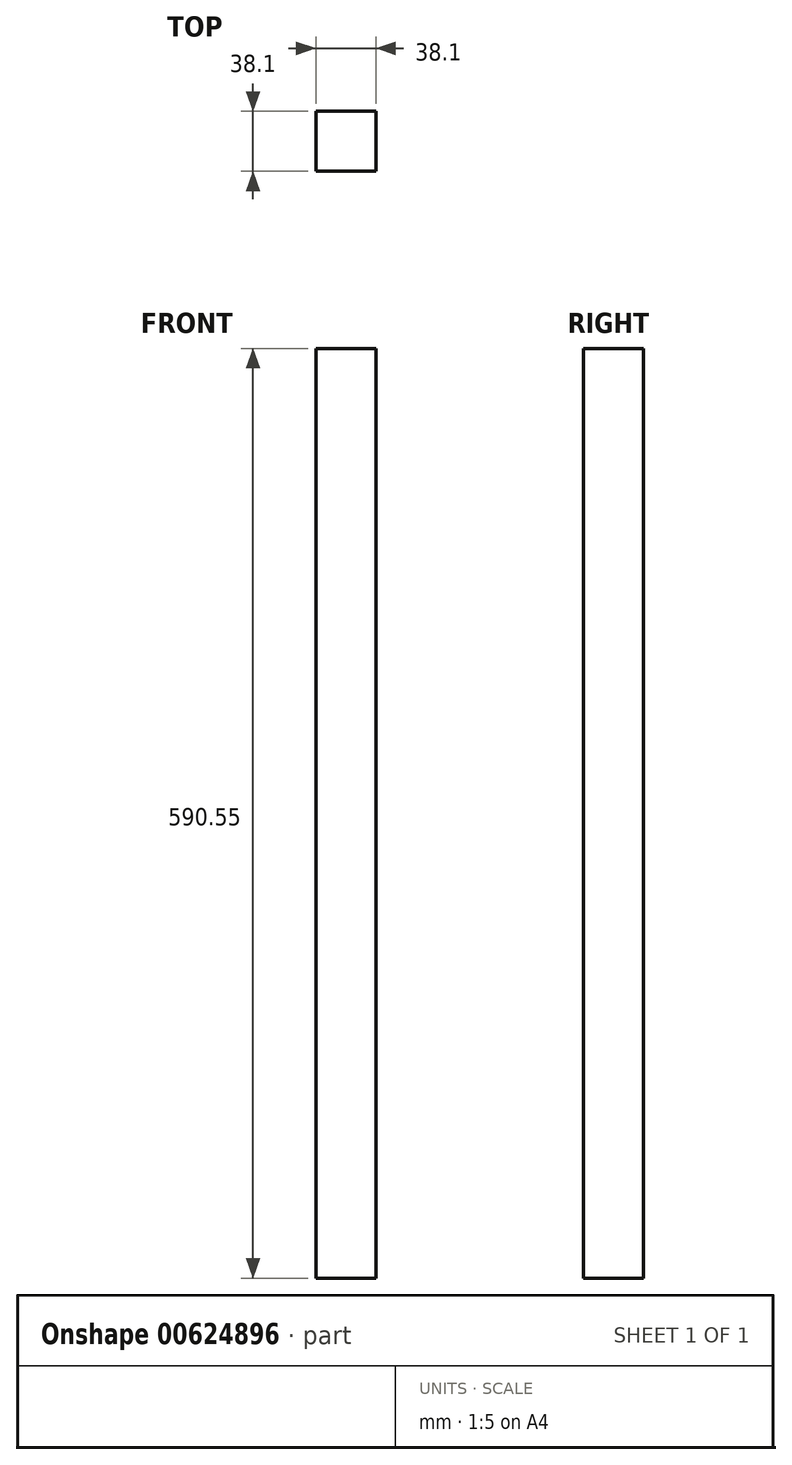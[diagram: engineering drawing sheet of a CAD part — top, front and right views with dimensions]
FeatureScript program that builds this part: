
annotation { "Feature Type Name" : "Feature", "Feature Type Description" : "" }
export const myFeature = defineFeature(function(context is Context, id is Id, definition is map)
    precondition{}
    {
        {
            var Q0;
            Q0=qCreatedBy(makeId("Top.planeOp"),FACE);
            var sketch = newSketch(context, id + "F0", { "sketchPlane" : qUnion([Q0])});
            skLineSegment(sketch, "E0.bottom", {"start": v(0, 0) * mm, "end": v(-38.1, 0) * mm});
            skLineSegment(sketch, "E0.top", {"start": v(0, -38.1) * mm, "end": v(-38.1, -38.1) * mm});
            skLineSegment(sketch, "E0.left", {"start": v(0, 0) * mm, "end": v(0, -38.1) * mm});
            skLineSegment(sketch, "E0.right", {"start": v(-38.1, 0) * mm, "end": v(-38.1, -38.1) * mm});
            skSolve(sketch);
        }
        {
            var Q0;
            Q0=makeQuery(id+"F0.imprint","IMPRINT",FACE,{"disambiguationData":[TD([[makeQuery(id+"F0.imprint","IMPRINT",EDGE,{"derivedFrom":sQuery(id+"F0.wireOp",EDGE,"E0.bottom")}),1.0]])]});
            extrude(context, id + "F1", {"entities" : qUnion([Q0]), "oppositeDirection" : true, "depth" : 590.55 * mm, "offsetDistance" : 25.4 * mm});
        }
    });
